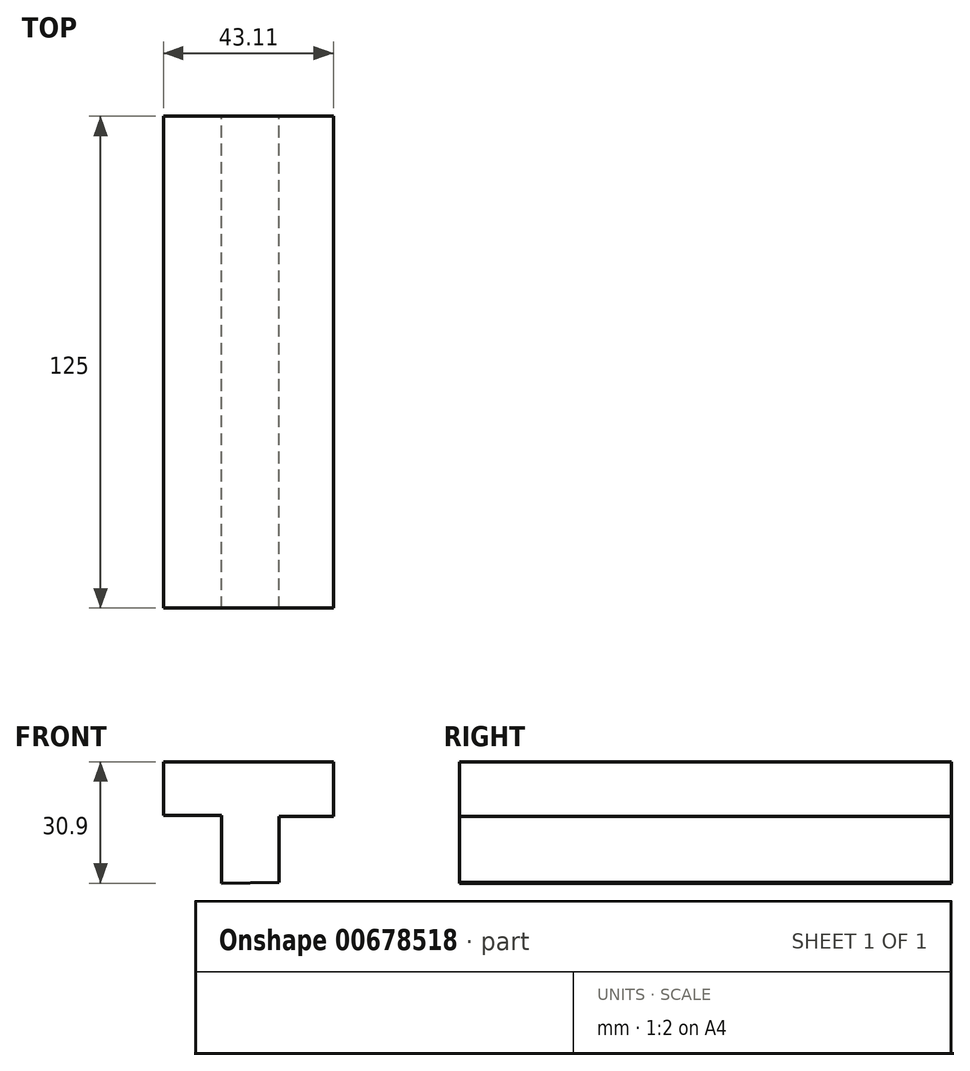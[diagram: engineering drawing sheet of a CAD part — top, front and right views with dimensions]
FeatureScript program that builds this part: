
annotation { "Feature Type Name" : "Feature", "Feature Type Description" : "" }
export const myFeature = defineFeature(function(context is Context, id is Id, definition is map)
    precondition{}
    {
        {
            var Q0;
            Q0=qCreatedBy(makeId("Front.planeOp"),FACE);
            var sketch = newSketch(context, id + "F0", { "sketchPlane" : qUnion([Q0])});
            skLineSegment(sketch, "E0", {"start": v(-17.96, 0) * mm, "end": v(25.15, 0) * mm});
            skLineSegment(sketch, "E1", {"start": v(-17.96, 0) * mm, "end": v(-17.96, -13.65) * mm});
            skLineSegment(sketch, "E2", {"start": v(25.15, 0) * mm, "end": v(25.15, -13.94) * mm});
            skLineSegment(sketch, "E3", {"start": v(-17.96, -13.65) * mm, "end": v(-3.3, -13.65) * mm});
            skLineSegment(sketch, "E4", {"start": v(25.15, -13.94) * mm, "end": v(11.35, -13.94) * mm});
            skLineSegment(sketch, "E5", {"start": v(-3.3, -13.65) * mm, "end": v(-3.3, -30.9) * mm});
            skLineSegment(sketch, "E6", {"start": v(11.35, -13.94) * mm, "end": v(11.35, -30.6) * mm});
            skLineSegment(sketch, "E7", {"start": v(-3.3, -30.9) * mm, "end": v(11.35, -30.6) * mm});
            skSolve(sketch);
        }
        {
            var Q0;
            Q0=makeQuery(id+"F0.imprint","IMPRINT",FACE,{"disambiguationData":[TD([[makeQuery(id+"F0.imprint","IMPRINT",EDGE,{"derivedFrom":sQuery(id+"F0.wireOp",EDGE,"E0")}),-1.0]])]});
            extrude(context, id + "F1", {"entities" : qUnion([Q0]), "depth" : 125 * mm, "offsetDistance" : 25 * mm});
        }
    });
